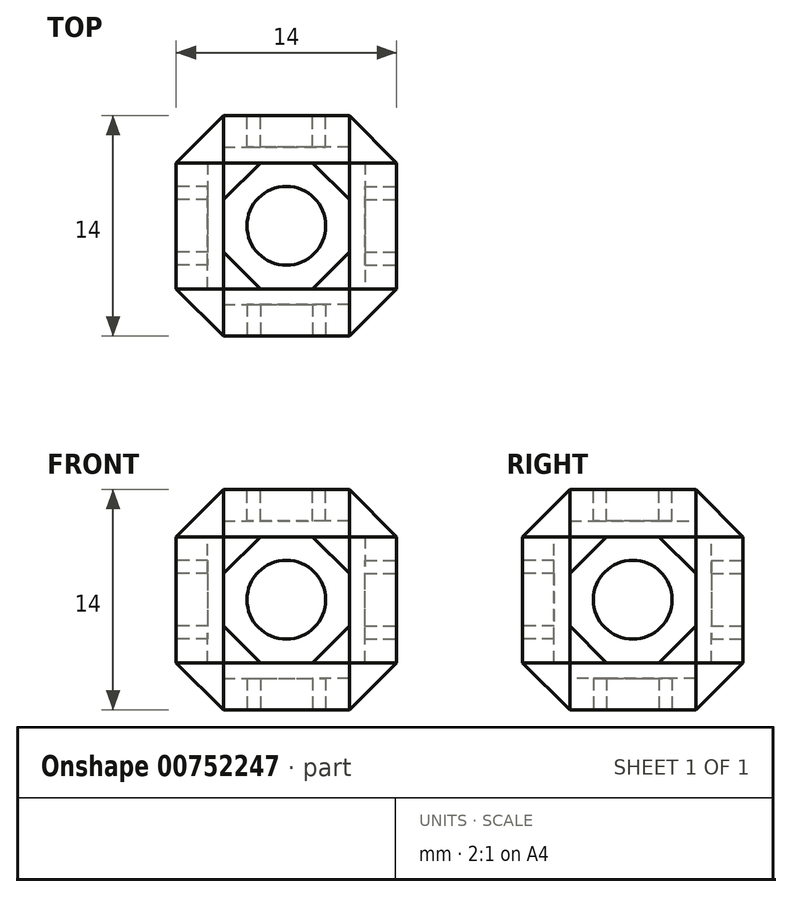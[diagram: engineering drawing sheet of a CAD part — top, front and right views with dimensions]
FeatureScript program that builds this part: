
annotation { "Feature Type Name" : "Feature", "Feature Type Description" : "" }
export const myFeature = defineFeature(function(context is Context, id is Id, definition is map)
    precondition{}
    {
        {
            var Q0;
            Q0=qCreatedBy(makeId("Top.planeOp"),FACE);
            var sketch = newSketch(context, id + "F0", { "sketchPlane" : qUnion([Q0])});
            skLineSegment(sketch, "E0.bottom", {"start": v(7, -7) * mm, "end": v(-7, -7) * mm});
            skLineSegment(sketch, "E0.top", {"start": v(7, 7) * mm, "end": v(-7, 7) * mm});
            skLineSegment(sketch, "E0.left", {"start": v(7, -7) * mm, "end": v(7, 7) * mm});
            skLineSegment(sketch, "E0.right", {"start": v(-7, -7) * mm, "end": v(-7, 7) * mm});
            skPoint(sketch, "E0.middle", {"position": v(0, 0) * mm});
            skSolve(sketch);
        }
        {
            var Q0;
            Q0=makeQuery(id+"F0.imprint","IMPRINT",FACE,{"disambiguationData":[TD([[makeQuery(id+"F0.imprint","IMPRINT",EDGE,{"derivedFrom":sQuery(id+"F0.wireOp",EDGE,"E0.bottom")}),-1.0]])]});
            extrude(context, id + "F1", {"entities" : qUnion([Q0]), "endBound" : BoundingType.SYMMETRIC, "depth" : 14 * mm, "offsetDistance" : 25 * mm});
        }
        {
            var Q0;
            Q0=makeQuery(id+"F1.opExtrude","SWEPT_FACE",FACE,{"disambiguationData":[OSD([sQuery(id+"F0.wireOp",EDGE,"E0.left")])]});
            var sketch = newSketch(context, id + "F2", { "sketchPlane" : qUnion([Q0])});
            skCircle(sketch, "E1.cCircle", {"center": v(0, 0) * mm, "radius": 4 * mm, "construction": true});
            skLineSegment(sketch, "E1.0", {"start": v(-4, -1.66) * mm, "end": v(-4, 1.66) * mm});
            skLineSegment(sketch, "E1.1", {"start": v(-4, 1.66) * mm, "end": v(-1.66, 4) * mm});
            skLineSegment(sketch, "E1.2", {"start": v(-1.66, 4) * mm, "end": v(1.66, 4) * mm});
            skLineSegment(sketch, "E1.3", {"start": v(1.66, 4) * mm, "end": v(4, 1.66) * mm});
            skLineSegment(sketch, "E1.4", {"start": v(4, 1.66) * mm, "end": v(4, -1.66) * mm});
            skLineSegment(sketch, "E1.5", {"start": v(4, -1.66) * mm, "end": v(1.66, -4) * mm});
            skLineSegment(sketch, "E1.6", {"start": v(1.66, -4) * mm, "end": v(-1.66, -4) * mm});
            skLineSegment(sketch, "E1.7", {"start": v(-1.66, -4) * mm, "end": v(-4, -1.66) * mm});
            skPoint(sketch, "E1.0.midPoint", {"position": v(-4, 0) * mm});
            skCircle(sketch, "E2", {"center": v(0, 0) * mm, "radius": 2.5 * mm});
            skSolve(sketch);
        }
        {
            var Q0;
            Q0=qCreatedBy(makeId("Front.planeOp"),FACE);
            var sketch = newSketch(context, id + "F3", { "sketchPlane" : qUnion([Q0])});
            skLineSegment(sketch, "E3", {"start": v(0, 0) * mm, "end": v(0, -10.81) * mm});
            skLineSegment(sketch, "E4", {"start": v(0, 0) * mm, "end": v(-9.79, 0) * mm});
            skSolve(sketch);
        }
        {
            var Q0;
            Q0 = qSketchRegion(id + "F2", true);
            extrude(context, id + "F4", {"entities" : qUnion([Q0]), "operationType" : NewBodyOperationType.REMOVE, "oppositeDirection" : true, "depth" : 2 * mm, "offsetDistance" : 25 * mm});
        }
        {
            var Q0;
            Q0=makeQuery(id+"F1.opExtrude","SWEPT_FACE",FACE,{"disambiguationData":[OSD([sQuery(id+"F0.wireOp",EDGE,"E0.top")])]});
            var Q1;
            Q1=makeQuery(id+"F1.opExtrude","CAP_FACE",FACE,{"disambiguationData":[OSD([sQuery(id+"F0.wireOp",EDGE,"E0.bottom"),sQuery(id+"F0.wireOp",EDGE,"E0.top"),sQuery(id+"F0.wireOp",EDGE,"E0.left"),sQuery(id+"F0.wireOp",EDGE,"E0.right")])],"isStart":false});
            var Q2;
            Q2=makeQuery(id+"F1.opExtrude","SWEPT_FACE",FACE,{"disambiguationData":[OSD([sQuery(id+"F0.wireOp",EDGE,"E0.bottom")])]});
            var Q3;
            Q3=makeQuery(id+"F1.opExtrude","CAP_FACE",FACE,{"disambiguationData":[OSD([sQuery(id+"F0.wireOp",EDGE,"E0.bottom"),sQuery(id+"F0.wireOp",EDGE,"E0.top"),sQuery(id+"F0.wireOp",EDGE,"E0.left"),sQuery(id+"F0.wireOp",EDGE,"E0.right")])],"isStart":true});
            chamfer(context, id + "F5", {"entities" : qUnion([Q0, Q1, Q2, Q3]), "width" : 3 * mm, "tangentPropagation" : true});
        }
        {
            var Q0;
            Q0=makeQuery(id+"F1.opExtrude","SWEPT_FACE",FACE,{"disambiguationData":[OSD([sQuery(id+"F0.wireOp",EDGE,"E0.top")])]});
            var sketch = newSketch(context, id + "F6", { "sketchPlane" : qUnion([Q0])});
            skCircle(sketch, "E5.cCircle", {"center": v(0, 0) * mm, "radius": 4 * mm, "construction": true});
            skLineSegment(sketch, "E5.0", {"start": v(-4, -1.66) * mm, "end": v(-4, 1.66) * mm});
            skLineSegment(sketch, "E5.1", {"start": v(-4, 1.66) * mm, "end": v(-1.66, 4) * mm});
            skLineSegment(sketch, "E5.2", {"start": v(-1.66, 4) * mm, "end": v(1.66, 4) * mm});
            skLineSegment(sketch, "E5.3", {"start": v(1.66, 4) * mm, "end": v(4, 1.66) * mm});
            skLineSegment(sketch, "E5.4", {"start": v(4, 1.66) * mm, "end": v(4, -1.66) * mm});
            skLineSegment(sketch, "E5.5", {"start": v(4, -1.66) * mm, "end": v(1.66, -4) * mm});
            skLineSegment(sketch, "E5.6", {"start": v(1.66, -4) * mm, "end": v(-1.66, -4) * mm});
            skLineSegment(sketch, "E5.7", {"start": v(-1.66, -4) * mm, "end": v(-4, -1.66) * mm});
            skPoint(sketch, "E5.0.midPoint", {"position": v(-4, 0) * mm});
            skCircle(sketch, "E6", {"center": v(0, 0) * mm, "radius": 2.5 * mm});
            skSolve(sketch);
        }
        {
            var Q0;
            Q0=makeQuery(id+"F1.opExtrude","CAP_FACE",FACE,{"disambiguationData":[OSD([sQuery(id+"F0.wireOp",EDGE,"E0.bottom"),sQuery(id+"F0.wireOp",EDGE,"E0.top"),sQuery(id+"F0.wireOp",EDGE,"E0.left"),sQuery(id+"F0.wireOp",EDGE,"E0.right")])],"isStart":false});
            var sketch = newSketch(context, id + "F7", { "sketchPlane" : qUnion([Q0])});
            skCircle(sketch, "E7.cCircle", {"center": v(0, 0) * mm, "radius": 4 * mm, "construction": true});
            skLineSegment(sketch, "E7.0", {"start": v(-4, -1.66) * mm, "end": v(-4, 1.66) * mm});
            skLineSegment(sketch, "E7.1", {"start": v(-4, 1.66) * mm, "end": v(-1.66, 4) * mm});
            skLineSegment(sketch, "E7.2", {"start": v(-1.66, 4) * mm, "end": v(1.66, 4) * mm});
            skLineSegment(sketch, "E7.3", {"start": v(1.66, 4) * mm, "end": v(4, 1.66) * mm});
            skLineSegment(sketch, "E7.4", {"start": v(4, 1.66) * mm, "end": v(4, -1.66) * mm});
            skLineSegment(sketch, "E7.5", {"start": v(4, -1.66) * mm, "end": v(1.66, -4) * mm});
            skLineSegment(sketch, "E7.6", {"start": v(1.66, -4) * mm, "end": v(-1.66, -4) * mm});
            skLineSegment(sketch, "E7.7", {"start": v(-1.66, -4) * mm, "end": v(-4, -1.66) * mm});
            skPoint(sketch, "E7.0.midPoint", {"position": v(-4, 0) * mm});
            skCircle(sketch, "E8", {"center": v(0, 0) * mm, "radius": 2.5 * mm});
            skSolve(sketch);
        }
        {
            var Q0;
            Q0=makeQuery(id+"F1.opExtrude","SWEPT_FACE",FACE,{"disambiguationData":[OSD([sQuery(id+"F0.wireOp",EDGE,"E0.right")])]});
            var sketch = newSketch(context, id + "F8", { "sketchPlane" : qUnion([Q0])});
            skCircle(sketch, "E9.cCircle", {"center": v(0, 0) * mm, "radius": 4 * mm, "construction": true});
            skLineSegment(sketch, "E9.0", {"start": v(-4, -1.66) * mm, "end": v(-4, 1.66) * mm});
            skLineSegment(sketch, "E9.1", {"start": v(-4, 1.66) * mm, "end": v(-1.66, 4) * mm});
            skLineSegment(sketch, "E9.2", {"start": v(-1.66, 4) * mm, "end": v(1.66, 4) * mm});
            skLineSegment(sketch, "E9.3", {"start": v(1.66, 4) * mm, "end": v(4, 1.66) * mm});
            skLineSegment(sketch, "E9.4", {"start": v(4, 1.66) * mm, "end": v(4, -1.66) * mm});
            skLineSegment(sketch, "E9.5", {"start": v(4, -1.66) * mm, "end": v(1.66, -4) * mm});
            skLineSegment(sketch, "E9.6", {"start": v(1.66, -4) * mm, "end": v(-1.66, -4) * mm});
            skLineSegment(sketch, "E9.7", {"start": v(-1.66, -4) * mm, "end": v(-4, -1.66) * mm});
            skPoint(sketch, "E9.0.midPoint", {"position": v(-4, 0) * mm});
            skCircle(sketch, "E10", {"center": v(0, 0) * mm, "radius": 2.5 * mm});
            skSolve(sketch);
        }
        {
            var Q0;
            Q0=makeQuery(id+"F1.opExtrude","SWEPT_FACE",FACE,{"disambiguationData":[OSD([sQuery(id+"F0.wireOp",EDGE,"E0.bottom")])]});
            var sketch = newSketch(context, id + "F9", { "sketchPlane" : qUnion([Q0])});
            skCircle(sketch, "E11.cCircle", {"center": v(0, 0) * mm, "radius": 4 * mm, "construction": true});
            skLineSegment(sketch, "E11.0", {"start": v(-4, -1.66) * mm, "end": v(-4, 1.66) * mm});
            skLineSegment(sketch, "E11.1", {"start": v(-4, 1.66) * mm, "end": v(-1.66, 4) * mm});
            skLineSegment(sketch, "E11.2", {"start": v(-1.66, 4) * mm, "end": v(1.66, 4) * mm});
            skLineSegment(sketch, "E11.3", {"start": v(1.66, 4) * mm, "end": v(4, 1.66) * mm});
            skLineSegment(sketch, "E11.4", {"start": v(4, 1.66) * mm, "end": v(4, -1.66) * mm});
            skLineSegment(sketch, "E11.5", {"start": v(4, -1.66) * mm, "end": v(1.66, -4) * mm});
            skLineSegment(sketch, "E11.6", {"start": v(1.66, -4) * mm, "end": v(-1.66, -4) * mm});
            skLineSegment(sketch, "E11.7", {"start": v(-1.66, -4) * mm, "end": v(-4, -1.66) * mm});
            skPoint(sketch, "E11.0.midPoint", {"position": v(-4, 0) * mm});
            skCircle(sketch, "E12", {"center": v(0, 0) * mm, "radius": 2.5 * mm});
            skSolve(sketch);
        }
        {
            var Q0;
            Q0=makeQuery(id+"F1.opExtrude","CAP_FACE",FACE,{"disambiguationData":[OSD([sQuery(id+"F0.wireOp",EDGE,"E0.bottom"),sQuery(id+"F0.wireOp",EDGE,"E0.top"),sQuery(id+"F0.wireOp",EDGE,"E0.left"),sQuery(id+"F0.wireOp",EDGE,"E0.right")])],"isStart":true});
            var sketch = newSketch(context, id + "F10", { "sketchPlane" : qUnion([Q0])});
            skCircle(sketch, "E13.cCircle", {"center": v(0, 0) * mm, "radius": 4 * mm, "construction": true});
            skLineSegment(sketch, "E13.0", {"start": v(-4, -1.66) * mm, "end": v(-4, 1.66) * mm});
            skLineSegment(sketch, "E13.1", {"start": v(-4, 1.66) * mm, "end": v(-1.66, 4) * mm});
            skLineSegment(sketch, "E13.2", {"start": v(-1.66, 4) * mm, "end": v(1.66, 4) * mm});
            skLineSegment(sketch, "E13.3", {"start": v(1.66, 4) * mm, "end": v(4, 1.66) * mm});
            skLineSegment(sketch, "E13.4", {"start": v(4, 1.66) * mm, "end": v(4, -1.66) * mm});
            skLineSegment(sketch, "E13.5", {"start": v(4, -1.66) * mm, "end": v(1.66, -4) * mm});
            skLineSegment(sketch, "E13.6", {"start": v(1.66, -4) * mm, "end": v(-1.66, -4) * mm});
            skLineSegment(sketch, "E13.7", {"start": v(-1.66, -4) * mm, "end": v(-4, -1.66) * mm});
            skPoint(sketch, "E13.0.midPoint", {"position": v(-4, 0) * mm});
            skCircle(sketch, "E14", {"center": v(0, 0) * mm, "radius": 2.5 * mm});
            skSolve(sketch);
        }
        {
            var Q0;
            Q0 = qSketchRegion(id + "F6", true);
            extrude(context, id + "F11", {"entities" : qUnion([Q0]), "operationType" : NewBodyOperationType.REMOVE, "oppositeDirection" : true, "depth" : 2 * mm, "offsetDistance" : 25 * mm});
        }
        {
            var Q0;
            Q0 = qSketchRegion(id + "F7", true);
            extrude(context, id + "F12", {"entities" : qUnion([Q0]), "operationType" : NewBodyOperationType.REMOVE, "oppositeDirection" : true, "depth" : 2 * mm, "offsetDistance" : 25 * mm});
        }
        {
            var Q0;
            Q0 = qSketchRegion(id + "F8", true);
            extrude(context, id + "F13", {"entities" : qUnion([Q0]), "operationType" : NewBodyOperationType.REMOVE, "oppositeDirection" : true, "depth" : 2 * mm, "offsetDistance" : 25 * mm});
        }
        {
            var Q0;
            Q0 = qSketchRegion(id + "F9", true);
            extrude(context, id + "F14", {"entities" : qUnion([Q0]), "operationType" : NewBodyOperationType.REMOVE, "oppositeDirection" : true, "depth" : 2 * mm, "offsetDistance" : 25 * mm});
        }
        {
            var Q0;
            Q0 = qSketchRegion(id + "F10", true);
            extrude(context, id + "F15", {"entities" : qUnion([Q0]), "operationType" : NewBodyOperationType.REMOVE, "oppositeDirection" : true, "depth" : 2 * mm, "offsetDistance" : 25 * mm});
        }
    });
